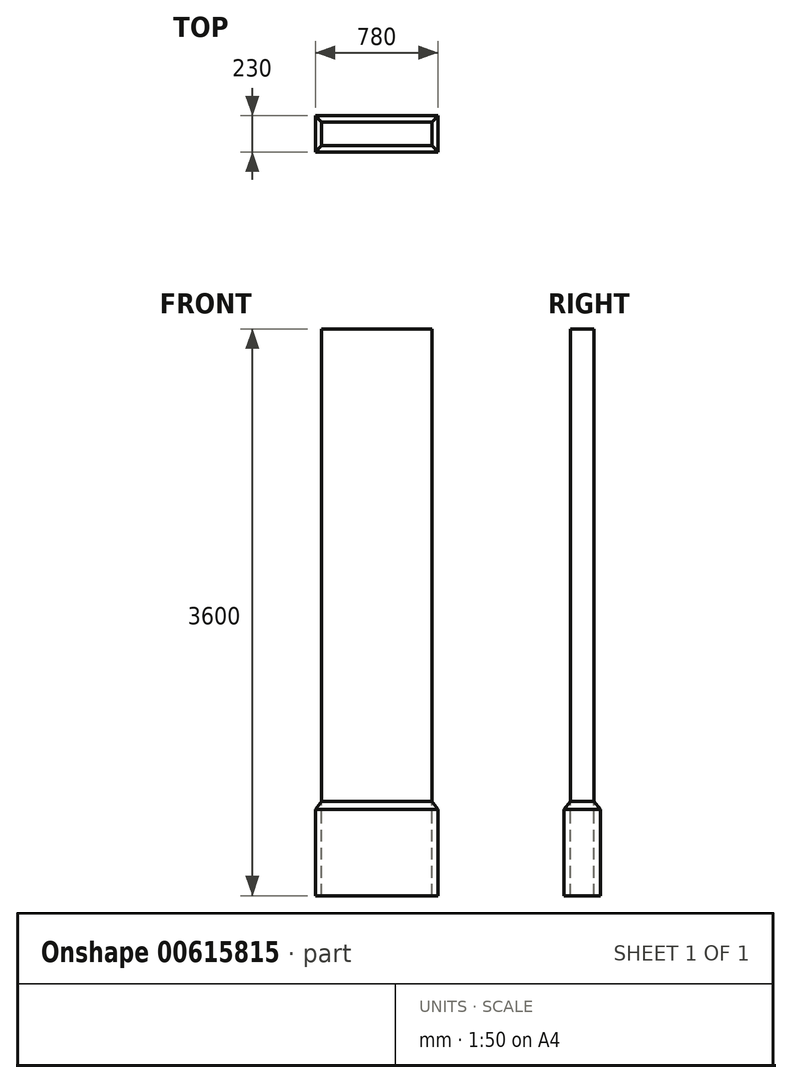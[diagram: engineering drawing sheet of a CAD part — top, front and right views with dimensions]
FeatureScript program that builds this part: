
annotation { "Feature Type Name" : "Feature", "Feature Type Description" : "" }
export const myFeature = defineFeature(function(context is Context, id is Id, definition is map)
    precondition{}
    {
        {
            var Q0;
            Q0=qCreatedBy(makeId("Top.planeOp"),FACE);
            var sketch = newSketch(context, id + "F0", { "sketchPlane" : qUnion([Q0])});
            skLineSegment(sketch, "E0.bottom", {"start": v(350, 75) * mm, "end": v(-350, 75) * mm});
            skLineSegment(sketch, "E0.top", {"start": v(350, -75) * mm, "end": v(-350, -75) * mm});
            skLineSegment(sketch, "E0.left", {"start": v(350, 75) * mm, "end": v(350, -75) * mm});
            skLineSegment(sketch, "E0.right", {"start": v(-350, 75) * mm, "end": v(-350, -75) * mm});
            skPoint(sketch, "E0.middle", {"position": v(0, 0) * mm});
            skLineSegment(sketch, "E1.0", {"start": v(-390, 115) * mm, "end": v(-390, -115) * mm});
            skLineSegment(sketch, "E1.1", {"start": v(390, 115) * mm, "end": v(-390, 115) * mm});
            skLineSegment(sketch, "E1.2", {"start": v(390, 115) * mm, "end": v(390, -115) * mm});
            skLineSegment(sketch, "E1.3", {"start": v(390, -115) * mm, "end": v(-390, -115) * mm});
            skSolve(sketch);
        }
        {
            var Q0;
            Q0=makeQuery(id+"F0.imprint","IMPRINT",FACE,{"disambiguationData":[TD([[makeQuery(id+"F0.imprint","IMPRINT",EDGE,{"derivedFrom":sQuery(id+"F0.wireOp",EDGE,"E0.bottom")}),1.0]])]});
            extrude(context, id + "F1", {"entities" : qUnion([Q0]), "depth" : 3000 * mm, "offsetDistance" : 25 * mm});
        }
        {
            var Q0;
            Q0=makeQuery(id+"F0.imprint","IMPRINT",FACE,{"disambiguationData":[TD([[makeQuery(id+"F0.imprint","IMPRINT",EDGE,{"derivedFrom":sQuery(id+"F0.wireOp",EDGE,"E0.bottom")}),-1.0]])]});
            extrude(context, id + "F2", {"entities" : qUnion([Q0]), "oppositeDirection" : true, "depth" : 600 * mm, "offsetDistance" : 25 * mm});
        }
        {
            var Q0;
            Q0=makeQuery(id+"F2.opExtrude","CAP_EDGE",EDGE,{"disambiguationData":[OSD([sQuery(id+"F0.wireOp",EDGE,"E1.3")])],"isStart":true});
            var Q1;
            Q1=makeQuery(id+"F2.opExtrude","CAP_EDGE",EDGE,{"disambiguationData":[OSD([sQuery(id+"F0.wireOp",EDGE,"E1.2")])],"isStart":true});
            var Q2;
            Q2=makeQuery(id+"F2.opExtrude","CAP_EDGE",EDGE,{"disambiguationData":[OSD([sQuery(id+"F0.wireOp",EDGE,"E1.0")])],"isStart":true});
            var Q3;
            Q3=makeQuery(id+"F2.opExtrude","CAP_EDGE",EDGE,{"disambiguationData":[OSD([sQuery(id+"F0.wireOp",EDGE,"E1.1")])],"isStart":true});
            chamfer(context, id + "F3", {"entities" : qUnion([Q0, Q1, Q2, Q3]), "chamferType" : ChamferType.TWO_OFFSETS, "width1" : 50 * mm, "oppositeDirection" : false, "width2" : 40 * mm});
        }
    });
